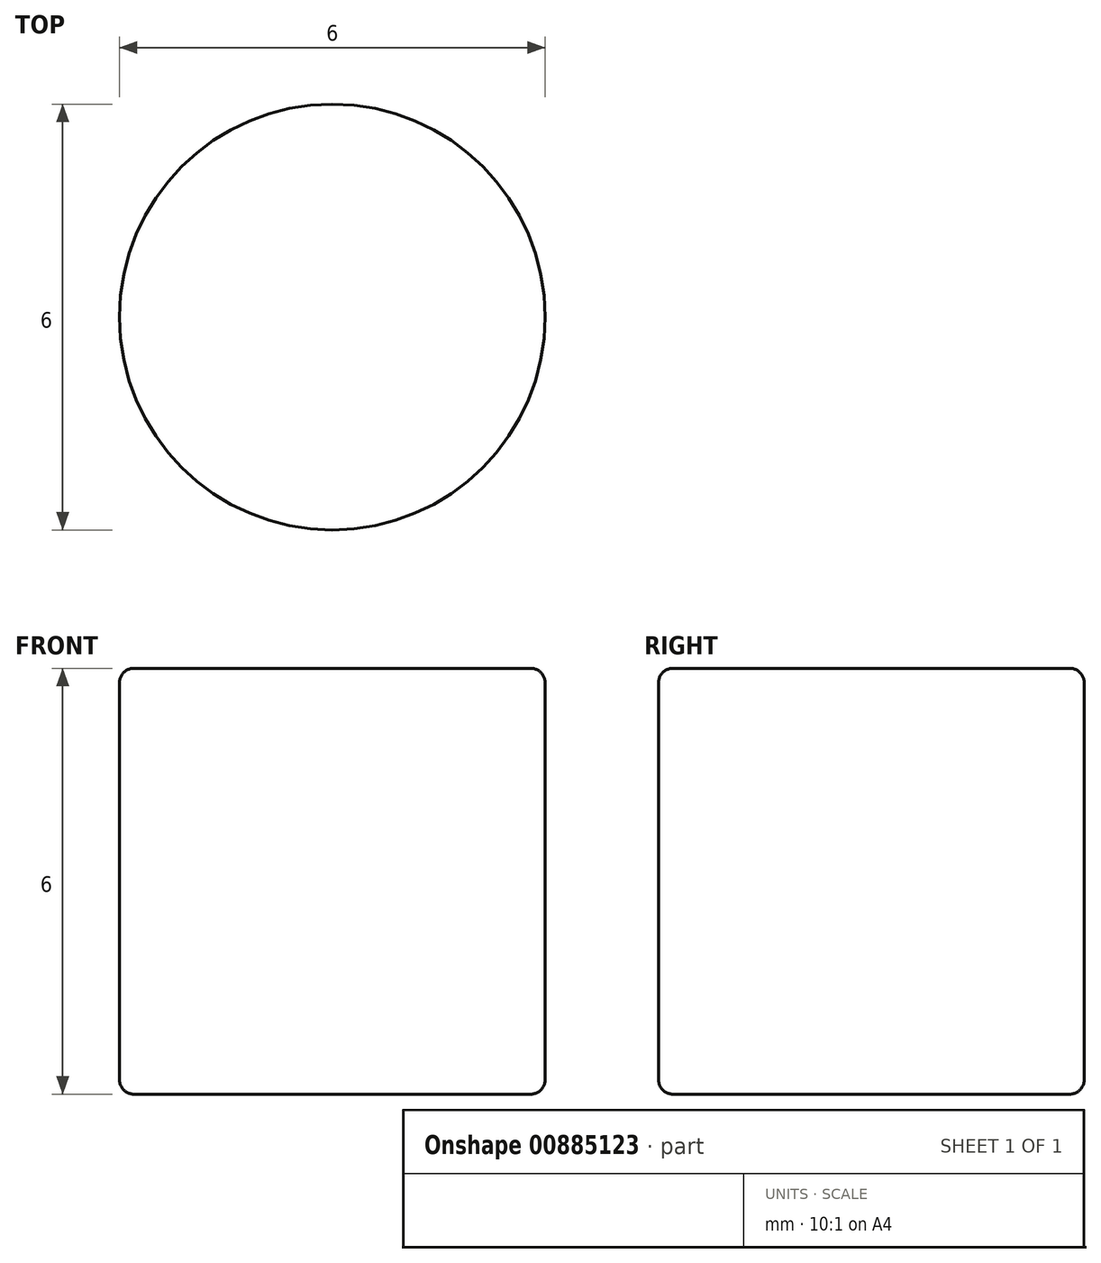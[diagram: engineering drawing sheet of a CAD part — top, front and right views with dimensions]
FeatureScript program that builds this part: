
annotation { "Feature Type Name" : "Feature", "Feature Type Description" : "" }
export const myFeature = defineFeature(function(context is Context, id is Id, definition is map)
    precondition{}
    {
        {
            var Q0;
            Q0=qCreatedBy(makeId("Top.planeOp"),FACE);
            var sketch = newSketch(context, id + "F0", { "sketchPlane" : qUnion([Q0])});
            skCircle(sketch, "E0", {"center": v(0, 0) * mm, "radius": 3 * mm});
            skSolve(sketch);
        }
        {
            var Q0;
            Q0 = qSketchRegion(id + "F0", true);
            extrude(context, id + "F1", {"entities" : qUnion([Q0]), "endBound" : BoundingType.SYMMETRIC, "depth" : 6 * mm, "offsetDistance" : 25 * mm});
        }
        {
            var Q0;
            Q0=makeQuery(id+"F1.opExtrude","CAP_FACE",FACE,{"disambiguationData":[OSD([sQuery(id+"F0.wireOp",EDGE,"E0")])],"isStart":false});
            var Q1;
            Q1=makeQuery(id+"F1.opExtrude","CAP_EDGE",EDGE,{"disambiguationData":[OSD([sQuery(id+"F0.wireOp",EDGE,"E0")])],"isStart":true});
            fillet(context, id + "F2", {"entities" : qUnion([Q0, Q1]), "radius" : 0.2 * mm, "tangentPropagation" : true, "allowEdgeOverflow" : false});
        }
    });
